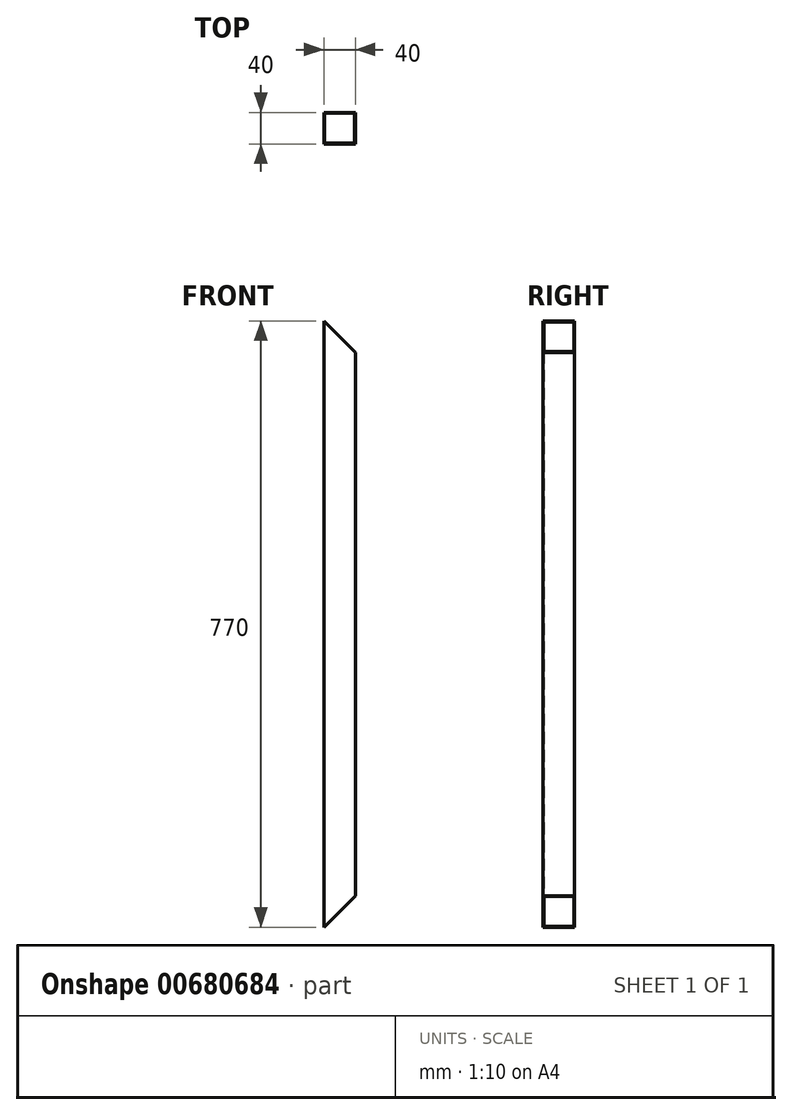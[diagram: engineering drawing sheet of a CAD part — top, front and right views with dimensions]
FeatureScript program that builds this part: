
annotation { "Feature Type Name" : "Feature", "Feature Type Description" : "" }
export const myFeature = defineFeature(function(context is Context, id is Id, definition is map)
    precondition{}
    {
        {
            var Q0;
            Q0=qCreatedBy(makeId("Top.planeOp"),FACE);
            var sketch = newSketch(context, id + "F0", { "sketchPlane" : qUnion([Q0])});
            skLineSegment(sketch, "E0.bottom", {"start": v(20, 20) * mm, "end": v(-20, 20) * mm});
            skLineSegment(sketch, "E0.top", {"start": v(20, -20) * mm, "end": v(-20, -20) * mm});
            skLineSegment(sketch, "E0.left", {"start": v(20, 20) * mm, "end": v(20, -20) * mm});
            skLineSegment(sketch, "E0.right", {"start": v(-20, 20) * mm, "end": v(-20, -20) * mm});
            skPoint(sketch, "E0.middle", {"position": v(0, 0) * mm});
            skLineSegment(sketch, "E1.bottom", {"start": v(19, 19) * mm, "end": v(-19, 19) * mm});
            skLineSegment(sketch, "E1.top", {"start": v(19, -19) * mm, "end": v(-19, -19) * mm});
            skLineSegment(sketch, "E1.left", {"start": v(19, 19) * mm, "end": v(19, -19) * mm});
            skLineSegment(sketch, "E1.right", {"start": v(-19, 19) * mm, "end": v(-19, -19) * mm});
            skSolve(sketch);
        }
        {
            var Q0;
            Q0=makeQuery(id+"F0.imprint","IMPRINT",FACE,{"disambiguationData":[TD([[makeQuery(id+"F0.imprint","IMPRINT",EDGE,{"derivedFrom":sQuery(id+"F0.wireOp",EDGE,"E0.bottom")}),1.0]])]});
            extrude(context, id + "F1", {"entities" : qUnion([Q0]), "endBound" : BoundingType.SYMMETRIC, "depth" : (900 - 60 - 60 - 10) * mm, "offsetDistance" : 25 * mm});
        }
        {
            var Q0;
            Q0=makeQuery(id+"F1.opExtrude","SWEPT_FACE",FACE,{"disambiguationData":[OSD([sQuery(id+"F0.wireOp",EDGE,"E0.top")])]});
            var sketch = newSketch(context, id + "F2", { "sketchPlane" : qUnion([Q0])});
            skLineSegment(sketch, "E2", {"start": v(-20, 385) * mm, "end": v(20, 345) * mm});
            skLineSegment(sketch, "E3", {"start": v(-20, -385) * mm, "end": v(20, -345) * mm});
            skSolve(sketch);
        }
        {
            var Q0;
            {var subQ0=sQuery(id+"F2.wireOp",EDGE,"E3");Q0=makeQuery(id+"F2.imprint","IMPRINT",FACE,{"disambiguationData":[TD([[makeQuery(id+"F2.imprint","IMPRINT",EDGE,{"derivedFrom":subQ0}),-1.0]])]});}
            var Q1;
            {var subQ0=sQuery(id+"F2.wireOp",EDGE,"E2");Q1=makeQuery(id+"F2.imprint","IMPRINT",FACE,{"disambiguationData":[TD([[makeQuery(id+"F2.imprint","IMPRINT",EDGE,{"derivedFrom":subQ0}),1.0]])]});}
            extrude(context, id + "F3", {"entities" : qUnion([Q0, Q1]), "operationType" : NewBodyOperationType.REMOVE, "oppositeDirection" : true, "depth" : 100 * mm, "offsetDistance" : 25 * mm});
        }
    });
